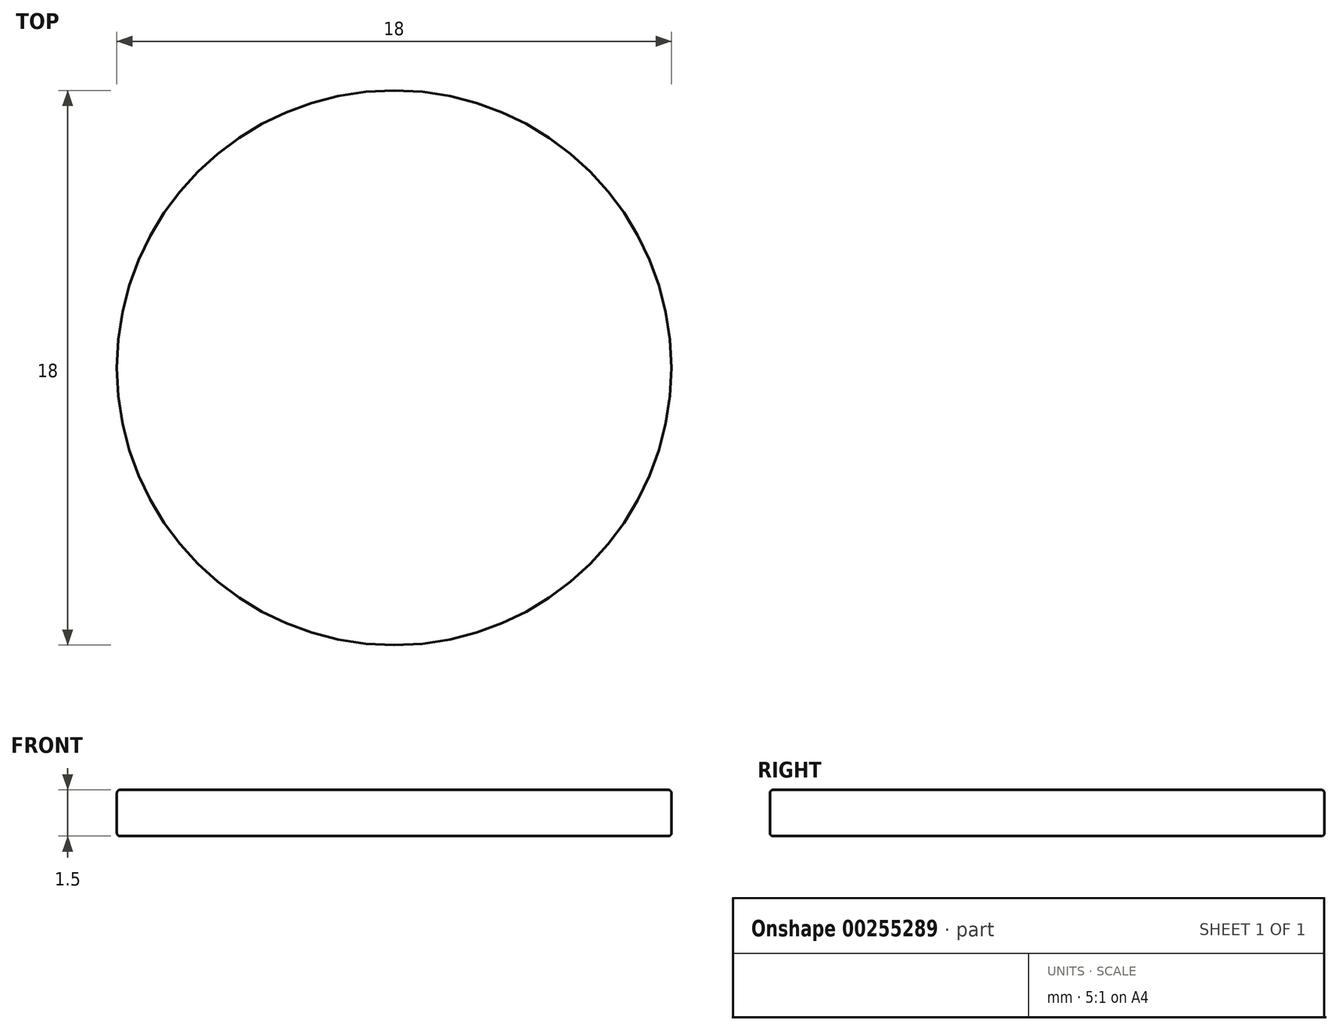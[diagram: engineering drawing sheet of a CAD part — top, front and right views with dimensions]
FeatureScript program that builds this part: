
annotation { "Feature Type Name" : "Feature", "Feature Type Description" : "" }
export const myFeature = defineFeature(function(context is Context, id is Id, definition is map)
    precondition{}
    {
        {
            var Q0;
            Q0=qCreatedBy(makeId("Top.planeOp"),FACE);
            var sketch = newSketch(context, id + "F0", { "sketchPlane" : qUnion([Q0])});
            skCircle(sketch, "E0", {"center": v(0, 0) * mm, "radius": 9 * mm});
            skSolve(sketch);
        }
        {
            var Q0;
            Q0=makeQuery(id+"F0.imprint","IMPRINT",FACE,{"disambiguationData":[TD([[makeQuery(id+"F0.imprint","IMPRINT",EDGE,{"derivedFrom":sQuery(id+"F0.wireOp",EDGE,"E0")}),1.0]])]});
            extrude(context, id + "F1", {"entities" : qUnion([Q0]), "depth" : 1.5 * mm});
        }
        {
            var Q0;
            Q0=makeQuery(id+"F1.opExtrude","CAP_FACE",FACE,{"disambiguationData":[OSD([sQuery(id+"F0.wireOp",EDGE,"E0")])],"isStart":false});
            fillet(context, id + "F2", {"entities" : qUnion([Q0]), "radius" : 0.1 * mm, "tangentPropagation" : true, "allowEdgeOverflow" : false});
        }
        {
            var Q0;
            Q0=makeQuery(id+"F1.opExtrude","CAP_FACE",FACE,{"disambiguationData":[OSD([sQuery(id+"F0.wireOp",EDGE,"E0")])],"isStart":true});
            fillet(context, id + "F3", {"entities" : qUnion([Q0]), "radius" : 0.1 * mm, "tangentPropagation" : true, "allowEdgeOverflow" : false});
        }
    });
